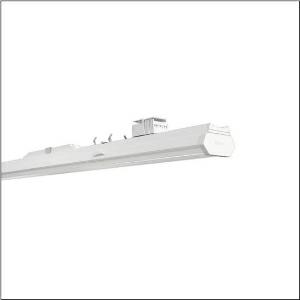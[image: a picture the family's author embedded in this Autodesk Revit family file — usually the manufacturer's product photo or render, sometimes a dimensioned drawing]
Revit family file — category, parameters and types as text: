
# Revit family: licross_21_protected_mo_52td12dn4a5gd
name_source: partatom
category: Lighting Fixtures
units: mm (PartAtom-declared; Revit-internal decimal feet)

## family parameters
Cut with Voids When Loaded = No
Host = Face
Light Source = No
Part Type = Normal
Room Calculation Point = No
Round Connector Dimension = Use Diameter
Shared = No

## types (1)
- --- (1 x LED, 1610 lm, 10.2 W, 4000K)
    Apparent Load = 10 VA
    CIE Flux Codes = 73 92 98 99 100
    Color Rendering = 80
    Color Temperature = 4000K
    Default Elevation = 1800 mm
    Description = Licross 21 Protected MO, luminaire insert, of sheet steel, galvanised, coil coated, white, length: 1.500mm, width: 90mm, height: 103mm, LED rated luminous flux: 10.700lm, light colour: 840, SDCM (Standard Deviation of Colour Matching)MacAdam ≤ 3 SDCM (initial), control gear: DALI 2 (for two DALI lines), with plug, 6-pole, with phase selection, mains connection: 220..240V, AC/DC, 0/50..60Hz, rated input power: 62W, without changeover relay, for emergency light function, for central battery installations according to EN 60598-2-22, internal wiring halogen-free, primary light control with lens, of plastic, primary optical cover: cover, of PMMA, light emission: direct distribution, primary light characteristic: symmetric, protection rating (complete): IP54, insulation class (complete): insulation class I (protective earthing), certification: CE, ENEC, VDE, UKCA, protection symbol: D if used in an environment with non-conductive dust loads with corresponding accessories, impact resistance: IK06, permissible ambient temperature for indoor applications: -25..+35°C, standard: EN 60598-2-22, corresponds to IFS (International Featured Standards) requirements for safety and quality in the food industry, reducing of maximum allowable ambient temperature of 5°C with ceiling mounting, LABS conformity tested according to VDMA 24364:2018-05, The light source and the operating device comply with the requirements of the Ecodesign Regulation (EU) 2019/2020 and are replaceable in accordance with this regulation, packaging unit: 1 piece
    Height = 92 mm
    Lamp = 1 x LED
    Lamp Light Flux = 1610 lm
    Lamp Power = 10.2 W
    Lamp count = 1
    Length = 1500 mm
    Luminous efficacy = 158 lm/W
    Manufacturer = Siteco
    ModVariant = No
    Model = 52TD12DN4A5GD
    Mounting Place = Ceiling
    Mounting Type = Pendant
    Number of Poles = 1
    OnlyDefault = Yes
    Power Factor = 1
    Product Name = Licross 21 Protected MO
    Product group = luminaire insert | ceiling pendant
    ProductGroupID = 901
    Protection Class = Protection class I
    Protection Degree = IP 54
    RLX_Detail_Level = 1
    RLX_Emergency_Light_Flux = 0 lm
    RLX_Emergency_Type = 0
    RLX_Emergency_Type_DB = No
    RlxData = <blob elided: 25181 chars, md5=d379510e>
    Socket = socket
    Standby Power = 0 W
    System Light Flux = 1610 lm
    System Power = 10 W
    Type Comments = : DC mode (central or group accumulator) initial emergency light level
    Type Image = l_1256148.jpg
    URL = http://relux.com
    VarID = @adj_116427
    Voltage = 0 V
    Weight = 0.00 kg
    Width = 88 mm

## geometry (parser evidence)
native form markers: Blend x4, Sweep x10
no freeform markers — native parametric forms only
